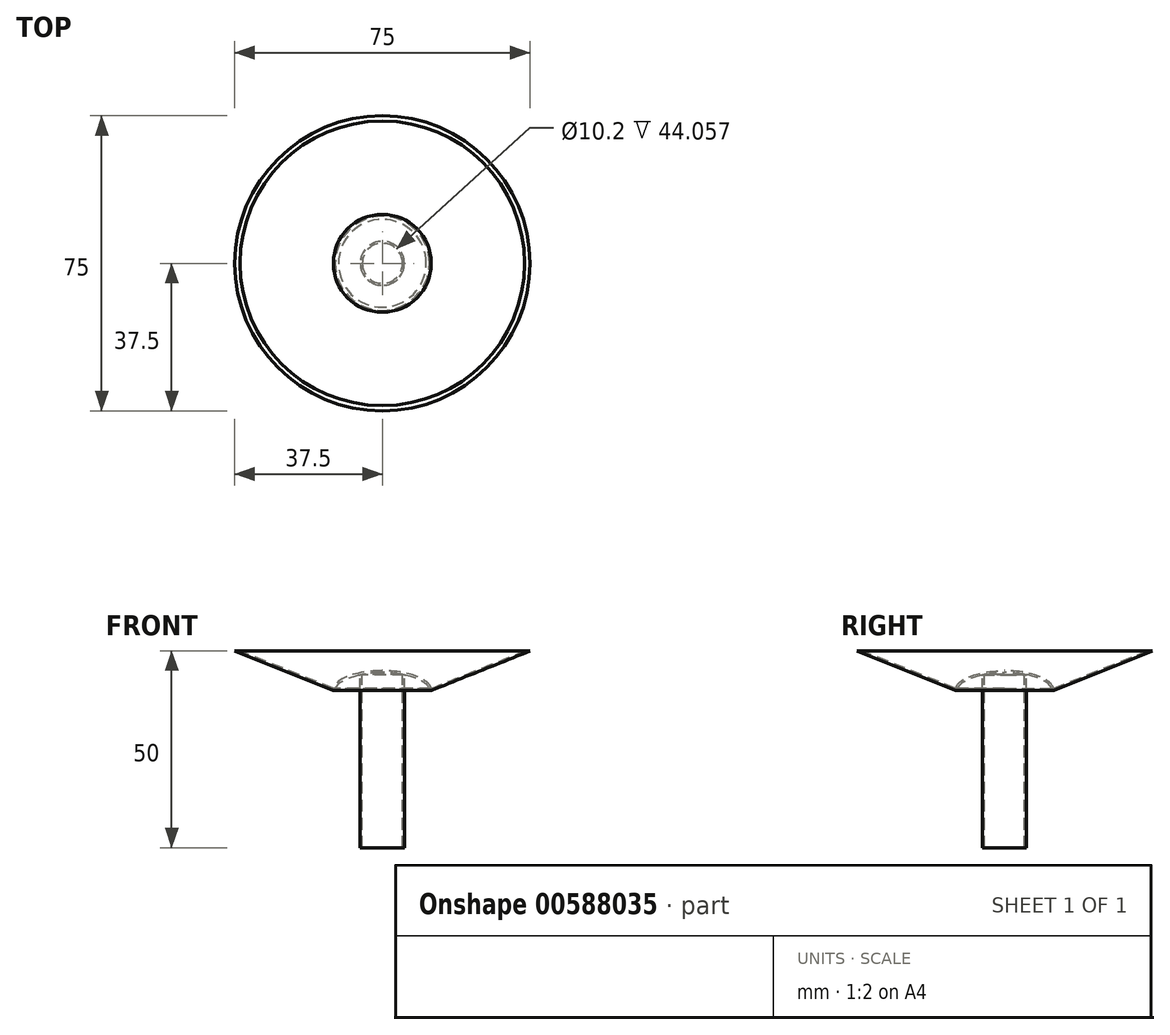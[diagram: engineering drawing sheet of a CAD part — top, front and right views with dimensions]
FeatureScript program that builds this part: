
annotation { "Feature Type Name" : "Feature", "Feature Type Description" : "" }
export const myFeature = defineFeature(function(context is Context, id is Id, definition is map)
    precondition{}
    {
        {
            var Q0;
            Q0=qCreatedBy(makeId("Top.planeOp"),FACE);
            var sketch = newSketch(context, id + "F0", { "sketchPlane" : qUnion([Q0])});
            skCircle(sketch, "E0", {"center": v(0, 0) * mm, "radius": 37.5 * mm});
            skSolve(sketch);
        }
        {
            var Q0;
            Q0=qCreatedBy(makeId("Top.planeOp"),FACE);
            cPlane(context, id + "F1", {"entities" : qUnion([Q0]), "cplaneType" : CPlaneType.OFFSET, "offset" : 10 * mm, "oppositeDirection" : true, "width" : 150 * mm, "height" : 150 * mm});
        }
        {
            var Q0;
            Q0=qCreatedBy(id+"F1.planeOp",FACE);
            var sketch = newSketch(context, id + "F2", { "sketchPlane" : qUnion([Q0])});
            skCircle(sketch, "E1", {"center": v(0, 0) * mm, "radius": 12.5 * mm});
            skSolve(sketch);
        }
        {
            var Q0;
            Q0=makeQuery(id+"F0.imprint","IMPRINT",FACE,{"disambiguationData":[TD([[makeQuery(id+"F0.imprint","IMPRINT",EDGE,{"derivedFrom":sQuery(id+"F0.wireOp",EDGE,"E0")}),1.0]])]});
            var Q1;
            Q1=makeQuery(id+"F2.imprint","IMPRINT",FACE,{"disambiguationData":[TD([[makeQuery(id+"F2.imprint","IMPRINT",EDGE,{"derivedFrom":sQuery(id+"F2.wireOp",EDGE,"E1")}),1.0]])]});
            loft(context, id + "F3", {"sheetProfilesArray" : [{ "sheetProfileEntities" : qUnion([Q0]) }, { "sheetProfileEntities" : qUnion([Q1]) }]});
        }
        {
            var Q0;
            Q0=makeQuery(id+"F3.opLoft","CAP_FACE",FACE,{"disambiguationData":[OSD([makeQuery(id+"F0.imprint","IMPRINT",FACE,{"disambiguationData":[TD([[makeQuery(id+"F0.imprint","IMPRINT",EDGE,{"derivedFrom":sQuery(id+"F0.wireOp",EDGE,"E0")}),1.0]])]})])],"isStart":true});
            shell(context, id + "F4", {"entities" : qUnion([Q0]), "thickness" : 0.5 * mm});
        }
        {
            var Q0;
            Q0=qCreatedBy(makeId("Front.planeOp"),FACE);
            var sketch = newSketch(context, id + "F5", { "sketchPlane" : qUnion([Q0])});
            skLineSegment(sketch, "E2", {"start": v(0, 0) * mm, "end": v(0, -20.21) * mm, "construction": true});
            skLineSegment(sketch, "E3", {"start": v(12.5, -10) * mm, "end": v(-12.5, -10) * mm, "construction": true});
            skEllipticalArc(sketch, "E4", {});
            skLineSegment(sketch, "E5", {"start": v(-12.5, -10) * mm, "end": v(0, -10) * mm});
            skLineSegment(sketch, "E6", {"start": v(0, -5) * mm, "end": v(0, -10) * mm});
            const initialGuessF5  = {"E4": [0, -0.01, 1, 0, 0.0125, 0.005, 1.5707963267948966, 3.141592653589793]};
            skSetInitialGuess(sketch, initialGuessF5);
            skSolve(sketch);
        }
        {
            var Q0;
            Q0=makeQuery(id+"F5.imprint","IMPRINT",FACE,{"disambiguationData":[TD([[makeQuery(id+"F5.imprint","IMPRINT",EDGE,{"derivedFrom":sQuery(id+"F5.wireOp",EDGE,"E4")}),1.0]])]});
            var Q1;
            Q1=sQuery(id+"F5.wireOp",EDGE,"E2");
            revolve(context, id + "F6", {"operationType" : NewBodyOperationType.ADD, "entities" : qUnion([Q0]), "axis" : qUnion([Q1]), "revolveType" : RevolveType.FULL});
        }
        {
            var Q0;
            Q0=makeQuery(id+"F3.opLoft","CAP_FACE",FACE,{"disambiguationData":[OSD([makeQuery(id+"F2.imprint","IMPRINT",FACE,{"disambiguationData":[TD([[makeQuery(id+"F2.imprint","IMPRINT",EDGE,{"derivedFrom":sQuery(id+"F2.wireOp",EDGE,"E1")}),1.0]])]})])],"isStart":true});
            shell(context, id + "F7", {"entities" : qUnion([Q0]), "thickness" : 0.5 * mm});
        }
        {
            var Q0;
            Q0=makeQuery(id+"F3.opLoft","CAP_FACE",FACE,{"disambiguationData":[OSD([makeQuery(id+"F2.imprint","IMPRINT",FACE,{"disambiguationData":[TD([[makeQuery(id+"F2.imprint","IMPRINT",EDGE,{"derivedFrom":sQuery(id+"F2.wireOp",EDGE,"E1")}),1.0]])]})])],"isStart":true});
            var sketch = newSketch(context, id + "F8", { "sketchPlane" : qUnion([Q0])});
            skCircle(sketch, "E7", {"center": v(0, 0) * mm, "radius": 5.1 * mm});
            skCircle(sketch, "E8.0", {"center": v(0, 0) * mm, "radius": 5.6 * mm});
            skSolve(sketch);
        }
        {
            var Q0;
            Q0=makeQuery(id+"F8.imprint","IMPRINT",FACE,{"disambiguationData":[TD([[makeQuery(id+"F8.imprint","IMPRINT",EDGE,{"derivedFrom":sQuery(id+"F8.wireOp",EDGE,"E7")}),-1.0]])]});
            extrude(context, id + "F9", {"entities" : qUnion([Q0]), "operationType" : NewBodyOperationType.ADD, "depth" : 40 * mm, "offsetDistance" : 25 * mm, "hasSecondDirection" : true, "secondDirectionOppositeDirection" : true, "secondDirectionDepth" : 4.4 * mm});
        }
    });
